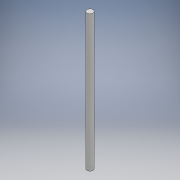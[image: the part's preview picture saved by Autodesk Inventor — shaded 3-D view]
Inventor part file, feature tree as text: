
AUTODESK INVENTOR PART (.ipt)
format: ipt  version: 2018 (Build 220112000, 112)  size: 90,624 bytes
history: native  units: mm
features: other x1, extrude x1, sketch x1
ambient origin geometry x8: Origin, YZ Plane, XZ Plane, XY Plane, X Axis, Y Axis, Z Axis, Center Point
bodies: Body1 (feature_tree)
feature tree (3):
  other  "ソリッド1"
  extrude  "押し出し1"  Depth=10.0mm
  sketch  "スケッチ1"
